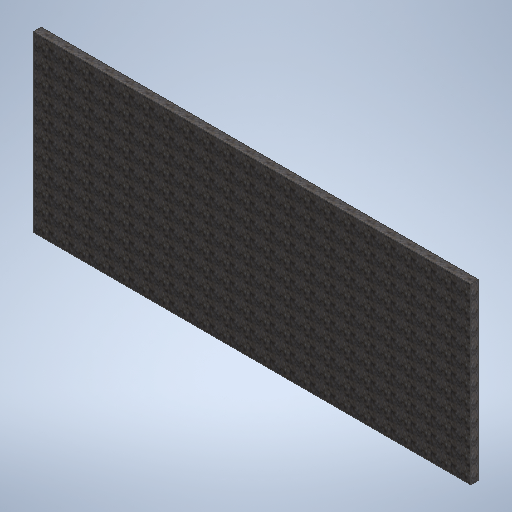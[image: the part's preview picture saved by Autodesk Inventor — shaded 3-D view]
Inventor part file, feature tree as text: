
AUTODESK INVENTOR PART (.ipt)
format: ipt  version: 2025.1 (Build 291241000, 241)  size: 389,632 bytes
history: native  units: mm
features: extrude x1, sketch x1
ambient origin geometry x8: Origin, YZ Plane, XZ Plane, XY Plane, X Axis, Y Axis, Z Axis, Center Point
bodies: Solid1 (feature_tree)
feature tree (2):
  extrude  "Extrusion1"  Depth=5000.0mm
  sketch  "Sketch1"  dims[d0=90.0mm d1=5000.0mm d2=1985.0mm d3=0.0mm]
